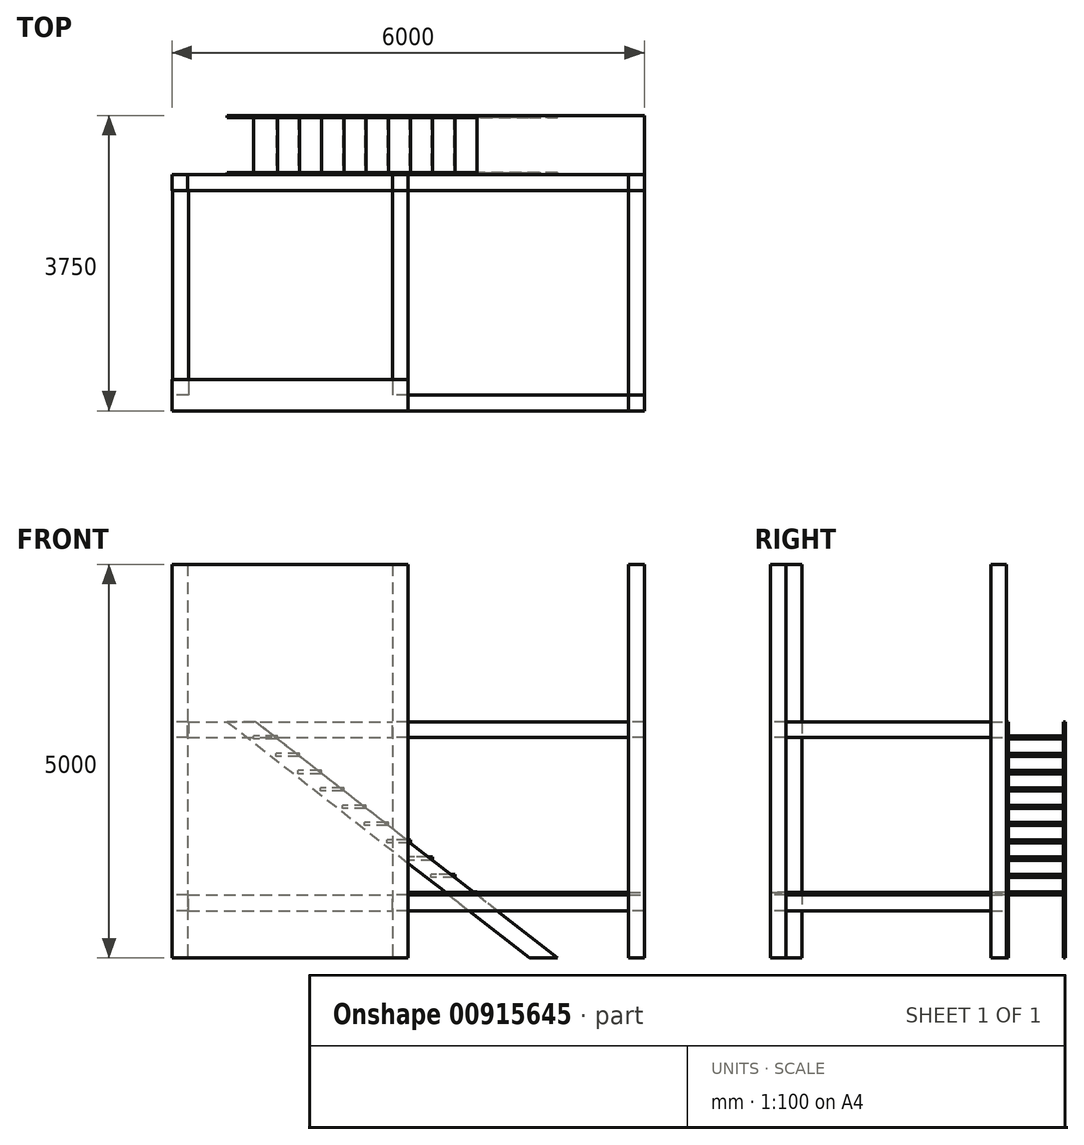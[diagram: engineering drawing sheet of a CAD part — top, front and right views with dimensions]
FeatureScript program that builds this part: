
annotation { "Feature Type Name" : "Feature", "Feature Type Description" : "" }
export const myFeature = defineFeature(function(context is Context, id is Id, definition is map)
    precondition{}
    {
        {
            var Q0;
            Q0=qCreatedBy(makeId("Top.planeOp"),FACE);
            var sketch = newSketch(context, id + "F0", { "sketchPlane" : qUnion([Q0])});
            skLineSegment(sketch, "E0.bottom", {"start": v(3000, -1500) * mm, "end": v(-3000, -1500) * mm});
            skLineSegment(sketch, "E0.top", {"start": v(3000, 1500) * mm, "end": v(-3000, 1500) * mm});
            skLineSegment(sketch, "E0.left", {"start": v(3000, -1500) * mm, "end": v(3000, 1500) * mm});
            skLineSegment(sketch, "E0.right", {"start": v(-3000, -1500) * mm, "end": v(-3000, 1500) * mm});
            skPoint(sketch, "E0.middle", {"position": v(0, 0) * mm});
            skSolve(sketch);
        }
        {
            var Q0;
            Q0=qCreatedBy(makeId("Top.planeOp"),FACE);
            var sketch = newSketch(context, id + "F1", { "sketchPlane" : qUnion([Q0])});
            skLineSegment(sketch, "E1.bottom", {"start": v(-3000, 1500) * mm, "end": v(-2800, 1500) * mm});
            skLineSegment(sketch, "E1.top", {"start": v(-3000, 1300) * mm, "end": v(-2800, 1300) * mm});
            skLineSegment(sketch, "E1.left", {"start": v(-3000, 1500) * mm, "end": v(-3000, 1300) * mm});
            skLineSegment(sketch, "E1.right", {"start": v(-2800, 1500) * mm, "end": v(-2800, 1300) * mm});
            skLineSegment(sketch, "E2.bottom", {"start": v(-200, 1300) * mm, "end": v(0, 1300) * mm});
            skLineSegment(sketch, "E2.top", {"start": v(-200, 1500) * mm, "end": v(0, 1500) * mm});
            skLineSegment(sketch, "E2.left", {"start": v(-200, 1300) * mm, "end": v(-200, 1500) * mm});
            skLineSegment(sketch, "E2.right", {"start": v(0, 1300) * mm, "end": v(0, 1500) * mm});
            skLineSegment(sketch, "E3.bottom", {"start": v(2800, 1300) * mm, "end": v(3000, 1300) * mm});
            skLineSegment(sketch, "E3.top", {"start": v(2800, 1500) * mm, "end": v(3000, 1500) * mm});
            skLineSegment(sketch, "E3.left", {"start": v(2800, 1300) * mm, "end": v(2800, 1500) * mm});
            skLineSegment(sketch, "E3.right", {"start": v(3000, 1300) * mm, "end": v(3000, 1500) * mm});
            skLineSegment(sketch, "E4.bottom", {"start": v(2800, -1300) * mm, "end": v(3000, -1300) * mm});
            skLineSegment(sketch, "E4.top", {"start": v(2800, -1500) * mm, "end": v(3000, -1500) * mm});
            skLineSegment(sketch, "E4.left", {"start": v(2800, -1300) * mm, "end": v(2800, -1500) * mm});
            skLineSegment(sketch, "E4.right", {"start": v(3000, -1300) * mm, "end": v(3000, -1500) * mm});
            skSolve(sketch);
        }
        {
            var Q0;
            Q0 = qSketchRegion(id + "F1", true);
            extrude(context, id + "F2", {"entities" : qUnion([Q0]), "depth" : 5000 * mm, "offsetDistance" : 25 * mm});
        }
        {
            var Q0;
            Q0=qCreatedBy(makeId("Top.planeOp"),FACE);
            var sketch = newSketch(context, id + "F3", { "sketchPlane" : qUnion([Q0])});
            skLineSegment(sketch, "E5.bottom", {"start": v(-3000, -1500) * mm, "end": v(0, -1500) * mm});
            skLineSegment(sketch, "E5.top", {"start": v(-3000, -1100) * mm, "end": v(0, -1100) * mm});
            skLineSegment(sketch, "E5.left", {"start": v(-3000, -1500) * mm, "end": v(-3000, -1100) * mm});
            skLineSegment(sketch, "E5.right", {"start": v(0, -1500) * mm, "end": v(0, -1100) * mm});
            skSolve(sketch);
        }
        {
            var Q0;
            Q0 = qSketchRegion(id + "F3", true);
            extrude(context, id + "F4", {"entities" : qUnion([Q0]), "depth" : 5000 * mm, "offsetDistance" : 25 * mm});
        }
        {
            var Q0;
            Q0=makeQuery(id+"F2.opExtrude","SWEPT_FACE",FACE,{"disambiguationData":[OSD([sQuery(id+"F1.wireOp",EDGE,"E4.bottom")])]});
            var sketch = newSketch(context, id + "F5", { "sketchPlane" : qUnion([Q0])});
            skLineSegment(sketch, "E6.bottom", {"start": v(-3000, 600) * mm, "end": v(-2800, 600) * mm});
            skLineSegment(sketch, "E6.top", {"start": v(-3000, 800) * mm, "end": v(-2800, 800) * mm});
            skLineSegment(sketch, "E6.left", {"start": v(-3000, 600) * mm, "end": v(-3000, 800) * mm});
            skLineSegment(sketch, "E6.right", {"start": v(-2800, 600) * mm, "end": v(-2800, 800) * mm});
            skLineSegment(sketch, "E7.bottom", {"start": v(0, 600) * mm, "end": v(200, 600) * mm});
            skLineSegment(sketch, "E7.top", {"start": v(0, 800) * mm, "end": v(200, 800) * mm});
            skLineSegment(sketch, "E7.left", {"start": v(0, 600) * mm, "end": v(0, 800) * mm});
            skLineSegment(sketch, "E7.right", {"start": v(200, 600) * mm, "end": v(200, 800) * mm});
            skLineSegment(sketch, "E8.bottom", {"start": v(2792.94, 600) * mm, "end": v(2992.94, 600) * mm});
            skLineSegment(sketch, "E8.top", {"start": v(2792.94, 800) * mm, "end": v(2992.94, 800) * mm});
            skLineSegment(sketch, "E8.left", {"start": v(2792.94, 600) * mm, "end": v(2792.94, 800) * mm});
            skLineSegment(sketch, "E8.right", {"start": v(2992.94, 600) * mm, "end": v(2992.94, 800) * mm});
            skSolve(sketch);
        }
        {
            var Q0;
            Q0 = qSketchRegion(id + "F5", true);
            extrude(context, id + "F6", {"entities" : qUnion([Q0]), "depth" : 2600 * mm, "offsetDistance" : 25 * mm});
        }
        {
            var Q0;
            Q0=makeQuery(id+"F2.opExtrude","SWEPT_FACE",FACE,{"disambiguationData":[OSD([sQuery(id+"F1.wireOp",EDGE,"E3.left")])]});
            var sketch = newSketch(context, id + "F7", { "sketchPlane" : qUnion([Q0])});
            skLineSegment(sketch, "E9.bottom", {"start": v(-1300, 800) * mm, "end": v(-1500, 800) * mm});
            skLineSegment(sketch, "E9.top", {"start": v(-1300, 600) * mm, "end": v(-1500, 600) * mm});
            skLineSegment(sketch, "E9.left", {"start": v(-1300, 800) * mm, "end": v(-1300, 600) * mm});
            skLineSegment(sketch, "E9.right", {"start": v(-1500, 800) * mm, "end": v(-1500, 600) * mm});
            skLineSegment(sketch, "E10.MirrorCS", {"start": v(1300, 600) * mm, "end": v(1500, 600) * mm});
            skLineSegment(sketch, "E11.MirrorCS", {"start": v(1500, 800) * mm, "end": v(1500, 600) * mm});
            skLineSegment(sketch, "E12.MirrorCS", {"start": v(1300, 800) * mm, "end": v(1500, 800) * mm});
            skLineSegment(sketch, "E13.MirrorCS", {"start": v(1300, 800) * mm, "end": v(1300, 600) * mm});
            skSolve(sketch);
        }
        {
            var Q0;
            Q0=makeQuery(id+"F7.imprint","IMPRINT",FACE,{"disambiguationData":[TD([[makeQuery(id+"F7.imprint","IMPRINT",EDGE,{"derivedFrom":sQuery(id+"F7.wireOp",EDGE,"E9.bottom")}),1.0]])]});
            var Q1;
            Q1=makeQuery(id+"F7.imprint","IMPRINT",FACE,{"disambiguationData":[TD([[makeQuery(id+"F7.imprint","IMPRINT",EDGE,{"derivedFrom":sQuery(id+"F7.wireOp",EDGE,"E10.MirrorCS")}),1.0]])]});
            extrude(context, id + "F8", {"entities" : qUnion([Q0, Q1]), "depth" : 2800 * mm, "offsetDistance" : 25 * mm});
        }
        {
            var Q0;
            Q0=makeQuery(id+"F2.opExtrude","SWEPT_FACE",FACE,{"disambiguationData":[OSD([sQuery(id+"F1.wireOp",EDGE,"E2.left")])]});
            var sketch = newSketch(context, id + "F9", { "sketchPlane" : qUnion([Q0])});
            skLineSegment(sketch, "E14.bottom", {"start": v(-1300, 800) * mm, "end": v(-1500, 800) * mm});
            skLineSegment(sketch, "E14.top", {"start": v(-1300, 600) * mm, "end": v(-1500, 600) * mm});
            skLineSegment(sketch, "E14.left", {"start": v(-1300, 800) * mm, "end": v(-1300, 600) * mm});
            skLineSegment(sketch, "E14.right", {"start": v(-1500, 800) * mm, "end": v(-1500, 600) * mm});
            skSolve(sketch);
        }
        {
            var Q0;
            Q0=makeQuery(id+"F9.imprint","IMPRINT",FACE,{"disambiguationData":[TD([[makeQuery(id+"F9.imprint","IMPRINT",EDGE,{"derivedFrom":sQuery(id+"F9.wireOp",EDGE,"E14.bottom")}),1.0]])]});
            extrude(context, id + "F10", {"entities" : qUnion([Q0]), "depth" : 2600 * mm, "offsetDistance" : 25 * mm});
        }
        {
            var Q0;
            Q0=makeQuery(id+"F0.imprint","IMPRINT",FACE,{"disambiguationData":[TD([[makeQuery(id+"F0.imprint","IMPRINT",EDGE,{"derivedFrom":sQuery(id+"F0.wireOp",EDGE,"E0.bottom")}),-1.0]])]});
            cPlane(context, id + "F11", {"entities" : qUnion([Q0]), "cplaneType" : CPlaneType.OFFSET, "offset" : 1800 * mm, "width" : 150 * mm, "height" : 150 * mm});
        }
        {
            var Q0;
            Q0=makeQuery(id+"F8.opExtrude","SWEPT_BODY",BODY,{"disambiguationData":[OSD([sQuery(id+"F7.wireOp",EDGE,"E10.MirrorCS"),sQuery(id+"F7.wireOp",EDGE,"E11.MirrorCS"),sQuery(id+"F7.wireOp",EDGE,"E12.MirrorCS"),sQuery(id+"F7.wireOp",EDGE,"E13.MirrorCS")])]});
            var Q1;
            Q1=makeQuery(id+"F6.opExtrude","SWEPT_BODY",BODY,{"disambiguationData":[OSD([sQuery(id+"F5.wireOp",EDGE,"E6.bottom"),sQuery(id+"F5.wireOp",EDGE,"E6.top"),sQuery(id+"F5.wireOp",EDGE,"E6.left"),sQuery(id+"F5.wireOp",EDGE,"E6.right")])]});
            var Q2;
            Q2=makeQuery(id+"F8.opExtrude","SWEPT_BODY",BODY,{"disambiguationData":[OSD([sQuery(id+"F7.wireOp",EDGE,"E9.bottom"),sQuery(id+"F7.wireOp",EDGE,"E9.top"),sQuery(id+"F7.wireOp",EDGE,"E9.left"),sQuery(id+"F7.wireOp",EDGE,"E9.right")])]});
            var Q3;
            Q3=makeQuery(id+"F6.opExtrude","SWEPT_BODY",BODY,{"disambiguationData":[OSD([sQuery(id+"F5.wireOp",EDGE,"E7.bottom"),sQuery(id+"F5.wireOp",EDGE,"E7.top"),sQuery(id+"F5.wireOp",EDGE,"E7.left"),sQuery(id+"F5.wireOp",EDGE,"E7.right")])]});
            var Q4;
            Q4=makeQuery(id+"F10.opExtrude","SWEPT_BODY",BODY,{"disambiguationData":[OSD([sQuery(id+"F9.wireOp",EDGE,"E14.bottom"),sQuery(id+"F9.wireOp",EDGE,"E14.top"),sQuery(id+"F9.wireOp",EDGE,"E14.left"),sQuery(id+"F9.wireOp",EDGE,"E14.right")])]});
            var Q5;
            Q5=makeQuery(id+"F6.opExtrude","SWEPT_BODY",BODY,{"disambiguationData":[OSD([sQuery(id+"F5.wireOp",EDGE,"E8.bottom"),sQuery(id+"F5.wireOp",EDGE,"E8.top"),sQuery(id+"F5.wireOp",EDGE,"E8.left"),sQuery(id+"F5.wireOp",EDGE,"E8.right")])]});
            var Q6;
            Q6=qCreatedBy(id+"F11.planeOp",FACE);
            mirror(context, id + "F12", {"entities" : qUnion([Q0, Q1, Q2, Q3, Q4, Q5]), "mirrorPlane" : qUnion([Q6])});
        }
        {
            var Q0;
            Q0=makeQuery(id+"F2.opExtrude","SWEPT_FACE",FACE,{"disambiguationData":[OSD([sQuery(id+"F1.wireOp",EDGE,"E2.top")])]});
            var sketch = newSketch(context, id + "F13", { "sketchPlane" : qUnion([Q0])});
            skLineSegment(sketch, "E15", {"start": v(-1897.16, 0) * mm, "end": v(1942.66, 3000) * mm});
            skLineSegment(sketch, "E16", {"start": v(1942.66, 3000) * mm, "end": v(2300, 3000) * mm});
            skLineSegment(sketch, "E17", {"start": v(2300, 3000) * mm, "end": v(-1539.82, 0) * mm});
            skLineSegment(sketch, "E18", {"start": v(-1539.82, 0) * mm, "end": v(-1897.16, 0) * mm});
            skSolve(sketch);
        }
        {
            var Q0;
            Q0 = qSketchRegion(id + "F13", true);
            extrude(context, id + "F14", {"entities" : qUnion([Q0]), "depth" : 25 * mm, "offsetDistance" : 25 * mm});
        }
        {
            var Q0;
            Q0=makeQuery(id+"F14.opExtrude","CAP_FACE",FACE,{"disambiguationData":[OSD([sQuery(id+"F13.wireOp",EDGE,"E15"),sQuery(id+"F13.wireOp",EDGE,"E16"),sQuery(id+"F13.wireOp",EDGE,"E17"),sQuery(id+"F13.wireOp",EDGE,"E18")])],"isStart":false});
            var sketch = newSketch(context, id + "F15", { "sketchPlane" : qUnion([Q0])});
            skLineSegment(sketch, "E19.bottom", {"start": v(-873.21, 800) * mm, "end": v(-573.21, 800) * mm});
            skLineSegment(sketch, "E19.top", {"start": v(-873.21, 840) * mm, "end": v(-573.21, 840) * mm});
            skLineSegment(sketch, "E19.left", {"start": v(-873.21, 800) * mm, "end": v(-873.21, 840) * mm});
            skLineSegment(sketch, "E19.right", {"start": v(-573.21, 800) * mm, "end": v(-573.21, 840) * mm});
            skLineSegment(sketch, "E20.0.1.0", {"start": v(-591.62, 1060) * mm, "end": v(-291.62, 1060) * mm});
            skLineSegment(sketch, "E20.0.1.1", {"start": v(-591.62, 1020) * mm, "end": v(-591.62, 1060) * mm});
            skLineSegment(sketch, "E20.0.1.2", {"start": v(-591.62, 1020) * mm, "end": v(-291.62, 1020) * mm});
            skLineSegment(sketch, "E20.0.1.3", {"start": v(-291.62, 1020) * mm, "end": v(-291.62, 1060) * mm});
            skLineSegment(sketch, "E20.0.2.0", {"start": v(-310.04, 1280) * mm, "end": v(-10.04, 1280) * mm});
            skLineSegment(sketch, "E20.0.2.1", {"start": v(-310.04, 1240) * mm, "end": v(-310.04, 1280) * mm});
            skLineSegment(sketch, "E20.0.2.2", {"start": v(-310.04, 1240) * mm, "end": v(-10.04, 1240) * mm});
            skLineSegment(sketch, "E20.0.2.3", {"start": v(-10.04, 1240) * mm, "end": v(-10.04, 1280) * mm});
            skLineSegment(sketch, "E20.0.3.0", {"start": v(-28.45, 1500) * mm, "end": v(271.55, 1500) * mm});
            skLineSegment(sketch, "E20.0.3.1", {"start": v(-28.45, 1460) * mm, "end": v(-28.45, 1500) * mm});
            skLineSegment(sketch, "E20.0.3.2", {"start": v(-28.45, 1460) * mm, "end": v(271.55, 1460) * mm});
            skLineSegment(sketch, "E20.0.3.3", {"start": v(271.55, 1460) * mm, "end": v(271.55, 1500) * mm});
            skLineSegment(sketch, "E20.0.4.0", {"start": v(253.14, 1720) * mm, "end": v(553.14, 1720) * mm});
            skLineSegment(sketch, "E20.0.4.1", {"start": v(253.14, 1680) * mm, "end": v(253.14, 1720) * mm});
            skLineSegment(sketch, "E20.0.4.2", {"start": v(253.14, 1680) * mm, "end": v(553.14, 1680) * mm});
            skLineSegment(sketch, "E20.0.4.3", {"start": v(553.14, 1680) * mm, "end": v(553.14, 1720) * mm});
            skLineSegment(sketch, "E20.0.5.0", {"start": v(534.72, 1940) * mm, "end": v(834.72, 1940) * mm});
            skLineSegment(sketch, "E20.0.5.1", {"start": v(534.72, 1900) * mm, "end": v(534.72, 1940) * mm});
            skLineSegment(sketch, "E20.0.5.2", {"start": v(534.72, 1900) * mm, "end": v(834.72, 1900) * mm});
            skLineSegment(sketch, "E20.0.5.3", {"start": v(834.72, 1900) * mm, "end": v(834.72, 1940) * mm});
            skLineSegment(sketch, "E20.0.6.0", {"start": v(816.31, 2160) * mm, "end": v(1116.31, 2160) * mm});
            skLineSegment(sketch, "E20.0.6.1", {"start": v(816.31, 2120) * mm, "end": v(816.31, 2160) * mm});
            skLineSegment(sketch, "E20.0.6.2", {"start": v(816.31, 2120) * mm, "end": v(1116.31, 2120) * mm});
            skLineSegment(sketch, "E20.0.6.3", {"start": v(1116.31, 2120) * mm, "end": v(1116.31, 2160) * mm});
            skLineSegment(sketch, "E20.0.7.0", {"start": v(1097.9, 2380) * mm, "end": v(1397.9, 2380) * mm});
            skLineSegment(sketch, "E20.0.7.1", {"start": v(1097.9, 2340) * mm, "end": v(1097.9, 2380) * mm});
            skLineSegment(sketch, "E20.0.7.2", {"start": v(1097.9, 2340) * mm, "end": v(1397.9, 2340) * mm});
            skLineSegment(sketch, "E20.0.7.3", {"start": v(1397.9, 2340) * mm, "end": v(1397.9, 2380) * mm});
            skLineSegment(sketch, "E20.0.8.0", {"start": v(1379.49, 2600) * mm, "end": v(1679.49, 2600) * mm});
            skLineSegment(sketch, "E20.0.8.1", {"start": v(1379.49, 2560) * mm, "end": v(1379.49, 2600) * mm});
            skLineSegment(sketch, "E20.0.8.2", {"start": v(1379.49, 2560) * mm, "end": v(1679.49, 2560) * mm});
            skLineSegment(sketch, "E20.0.8.3", {"start": v(1679.49, 2560) * mm, "end": v(1679.49, 2600) * mm});
            skLineSegment(sketch, "E20.0.9.0", {"start": v(1661.07, 2820) * mm, "end": v(1961.07, 2820) * mm});
            skLineSegment(sketch, "E20.0.9.1", {"start": v(1661.07, 2780) * mm, "end": v(1661.07, 2820) * mm});
            skLineSegment(sketch, "E20.0.9.2", {"start": v(1661.07, 2780) * mm, "end": v(1961.07, 2780) * mm});
            skLineSegment(sketch, "E20.0.9.3", {"start": v(1961.07, 2780) * mm, "end": v(1961.07, 2820) * mm});
            skLineSegment(sketch, "E20.direction1", {"start": v(-573.21, 840) * mm, "end": v(-474.01, 837.37) * mm, "construction": true});
            skLineSegment(sketch, "E20.direction2", {"start": v(-573.21, 840) * mm, "end": v(-291.62, 1060) * mm, "construction": true});
            skSolve(sketch);
        }
        {
            var Q0;
            Q0 = qSketchRegion(id + "F15", true);
            extrude(context, id + "F16", {"entities" : qUnion([Q0]), "depth" : 700 * mm, "offsetDistance" : 25 * mm});
        }
        {
            var Q0;
            Q0=makeQuery(id+"F14.opExtrude","CAP_FACE",FACE,{"disambiguationData":[OSD([sQuery(id+"F13.wireOp",EDGE,"E15"),sQuery(id+"F13.wireOp",EDGE,"E16"),sQuery(id+"F13.wireOp",EDGE,"E17"),sQuery(id+"F13.wireOp",EDGE,"E18")])],"isStart":false});
            cPlane(context, id + "F17", {"entities" : qUnion([Q0]), "cplaneType" : CPlaneType.OFFSET, "offset" : 350 * mm, "width" : 150 * mm, "height" : 150 * mm});
        }
        {
            var Q0;
            Q0=makeQuery(id+"F14.opExtrude","SWEPT_BODY",BODY,{"disambiguationData":[OSD([sQuery(id+"F13.wireOp",EDGE,"E15"),sQuery(id+"F13.wireOp",EDGE,"E16"),sQuery(id+"F13.wireOp",EDGE,"E17"),sQuery(id+"F13.wireOp",EDGE,"E18")])]});
            var Q1;
            Q1=qCreatedBy(id+"F17.planeOp",FACE);
            mirror(context, id + "F18", {"entities" : qUnion([Q0]), "mirrorPlane" : qUnion([Q1])});
        }
        {
            var Q0;
            Q0=makeQuery(id+"F6.opExtrude","SWEPT_FACE",FACE,{"disambiguationData":[OSD([sQuery(id+"F5.wireOp",EDGE,"E6.top")])]});
            var sketch = newSketch(context, id + "F19", { "sketchPlane" : qUnion([Q0])});
            skLineSegment(sketch, "E21", {"start": v(2800, -1500) * mm, "end": v(2800, -1300) * mm});
            skLineSegment(sketch, "E22", {"start": v(2800, -1300) * mm, "end": v(3000, -1300) * mm});
            skLineSegment(sketch, "E23", {"start": v(3000, -1300) * mm, "end": v(3000, 1300) * mm});
            skLineSegment(sketch, "E24", {"start": v(3000, 1300) * mm, "end": v(2800, 1300) * mm});
            skLineSegment(sketch, "E25", {"start": v(2800, 1300) * mm, "end": v(2800, 1500) * mm});
            skLineSegment(sketch, "E26", {"start": v(2800, 1500) * mm, "end": v(3000, 1500) * mm});
            skLineSegment(sketch, "E27", {"start": v(3000, 1500) * mm, "end": v(3000, 2250) * mm});
            skLineSegment(sketch, "E28", {"start": v(3000, 2250) * mm, "end": v(873.21, 2250) * mm});
            skLineSegment(sketch, "E29", {"start": v(873.21, 2250) * mm, "end": v(873.21, 1500) * mm});
            skLineSegment(sketch, "E30", {"start": v(873.21, 1500) * mm, "end": v(0, 1500) * mm});
            skLineSegment(sketch, "E31", {"start": v(0, 1500) * mm, "end": v(0, -1300) * mm});
            skLineSegment(sketch, "E32", {"start": v(0, -1300) * mm, "end": v(0, -1499.62) * mm});
            skLineSegment(sketch, "E33", {"start": v(0, -1499.62) * mm, "end": v(2800, -1500) * mm});
            skSolve(sketch);
        }
        {
            var Q0;
            Q0=makeQuery(id+"F19.imprint","IMPRINT",FACE,{"disambiguationData":[TD([[makeQuery(id+"F19.imprint","IMPRINT",EDGE,{"derivedFrom":sQuery(id+"F19.wireOp",EDGE,"E21")}),1.0]])]});
            extrude(context, id + "F20", {"entities" : qUnion([Q0]), "depth" : 30 * mm, "offsetDistance" : 25 * mm});
        }
    });
